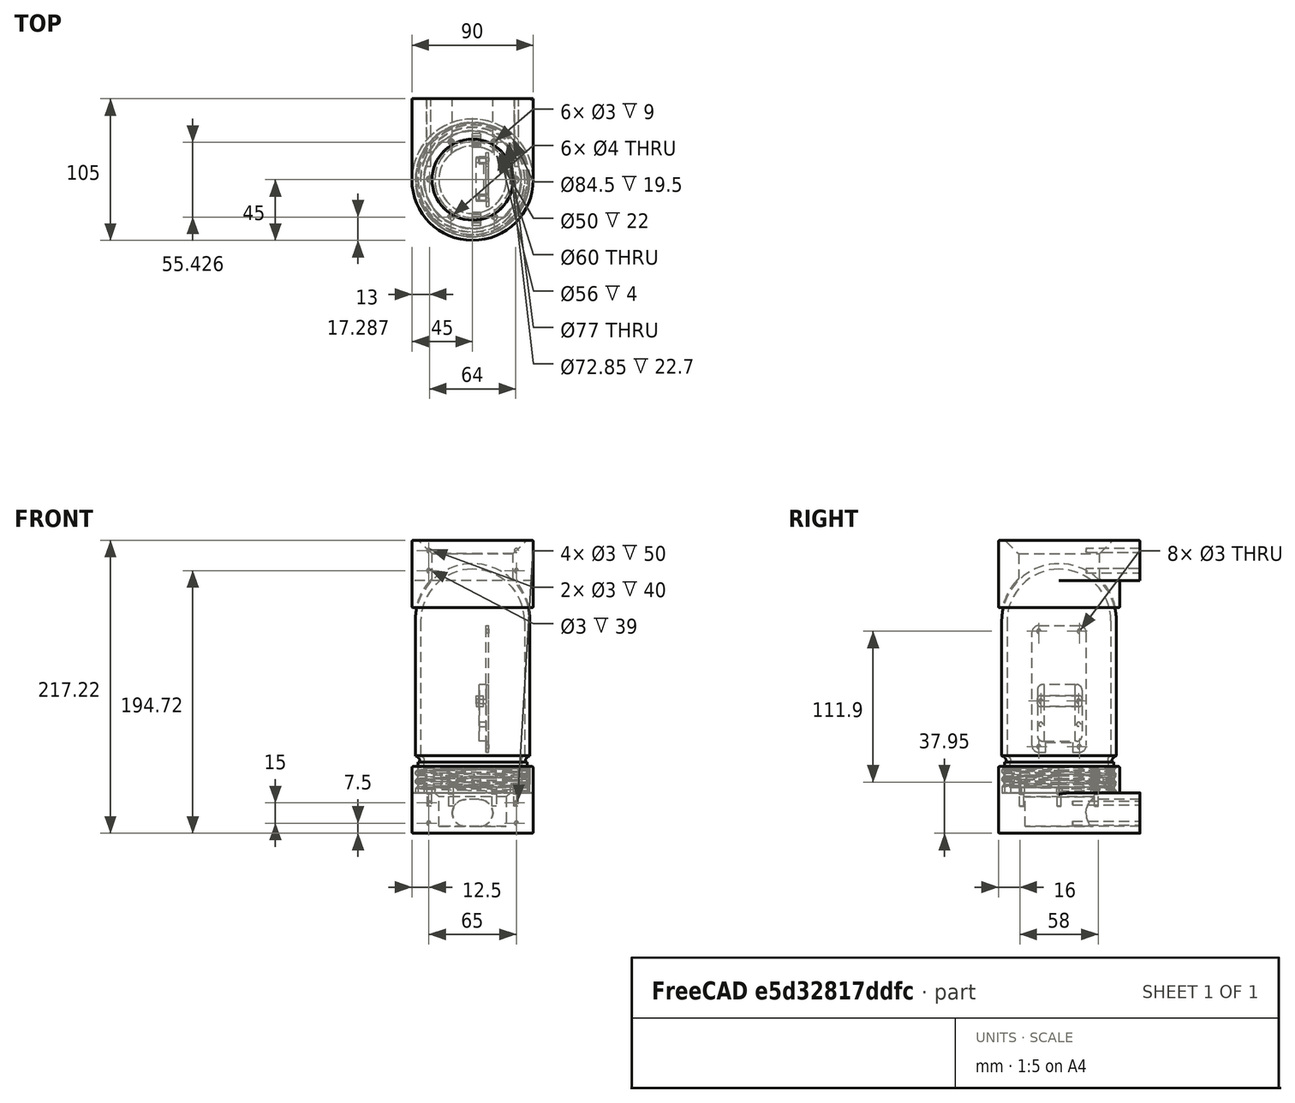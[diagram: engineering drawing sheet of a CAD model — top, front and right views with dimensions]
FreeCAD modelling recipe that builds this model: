
FCSTD DOCUMENT  (FreeCAD 0.19R)
Label: CrocSaintGerard_V5
License: All rights reserved
LicenseURL: http://en.wikipedia.org/wiki/All_rights_reserved
objects: Sketcher::SketchObject×36, PartDesign::Fillet×19, PartDesign::Pocket×18, PartDesign::Pad×14, PartDesign::Body×12, PartDesign::Chamfer×5, Mesh::Feature×4, PartDesign::Revolution×2, Part::Helix×1, PartDesign::ShapeBinder×1, PartDesign::AdditivePipe×1, PartDesign::LinearPattern×1, PartDesign::Groove×1, App::VRMLObject×1, App::MeasureDistance×1
note: 171 computed .brp shape members not serialized (recipe doc carries the construction recipe); baked Part::Feature solids carry a one-line shape summary decoded from their .brp

FEATURE [Part::Helix] Helix
  Angle = 0
  AttacherType = Attacher::AttachEngine3D
  Height = 6.22
  LocalCoord = 0
  Pitch = 6.23
  Radius = 40.5
  Style = 1
FEATURE [Sketcher::SketchObject] Sketch001  label="sketch_cylindre_base"
  FullyConstrained = true
  MapMode = 5
  Support = -> [XY_Plane]
  sketch-geometry (2):
    g0: Circle CenterX=0 CenterY=0 CenterZ=0 NormalX=0 NormalY=0 NormalZ=1 AngleXU=0 Radius=42.25
    g1: Circle CenterX=0 CenterY=0 CenterZ=0 NormalX=0 NormalY=0 NormalZ=1 AngleXU=0 Radius=45
  constraints (4):
    c: Coincident(g0,g-1)
    c: Coincident(g1,g0)
    c: Radius(g0) = 42.25
    c: Radius(g1) = 45
FEATURE [PartDesign::Pad] Pad  label="cylindre_base"
  Direction = (1,1,1)
  Length = 20
  Length2 = 100
  Profile = -> Sketch001
  Type = 0
FEATURE [Sketcher::SketchObject] Sketch002  label="sketch_profil_dent"
  FullyConstrained = true
  MapMode = 5
  Placement = pos=(0,0,0) rot=(1,0,0;1.5708rad)
  Support = -> [XZ_Plane]
  sketch-geometry (7):
    g0: LineSegment StartX=42.25 StartY=4.40427 StartZ=0 EndX=40.9557 EndY=3.11 EndZ=0
    g1: LineSegment StartX=40.9557 StartY=3.11 StartZ=0 EndX=40.9557 EndY=1.29427 EndZ=0
    g2: LineSegment StartX=40.9557 StartY=1.29427 StartZ=0 EndX=42.25 EndY=0 EndZ=0
    g3: LineSegment StartX=42.25 StartY=4.40427 StartZ=0 EndX=42.25 EndY=6.22 EndZ=0
    g4: LineSegment StartX=42.25 StartY=6.22 StartZ=0 EndX=43.25 EndY=6.22 EndZ=0
    g5: LineSegment StartX=43.25 StartY=6.22 StartZ=0 EndX=43.25 EndY=0 EndZ=0
    g6: LineSegment StartX=43.25 StartY=0 StartZ=0 EndX=42.25 EndY=0 EndZ=0
  constraints (21):
    c: Coincident(g0,g1)
    c: Vertical(g1)
    c: Coincident(g1,g2)
    c: DistanceX(g-2,g2) = 42.25
    c: PointOnObject(g2,g-1)
    c: Coincident(g0,g3)
    c: Vertical(g3)
    c: Coincident(g3,g4)
    c: Horizontal(g4)
    c: Coincident(g4,g5)
    c: PointOnObject(g5,g-1)
    c: Vertical(g5)
    c: Coincident(g5,g6)
    c: Coincident(g6,g2)
    c: DistanceX(g4,g4) = 1
    c: Equal(g3,g1)
    c: Equal(g2,g0)
    c: Angle(g2,g-1) = 0.785398
    c: Equal(g1,g3)
    c: DistanceY(g5,g5) = 6.22
    c: DistanceX(g-2,g0) = 42.25
FEATURE [PartDesign::ShapeBinder] ShapeBinder  label="ShapeBinder-helix"
  Support = -> [Helix]
  TraceSupport = false
FEATURE [PartDesign::AdditivePipe] AdditivePipe  label="filet"
  AuxilleryCurvelinear = true
  AuxillerySpineTangent = false
  BaseFeature = -> Pad
  Binormal = (0,0,0)
  Mode = 2
  Profile = -> Sketch002
  Spine = -> ShapeBinder
  SpineTangent = false
  Transformation = 0
  Transition = 0
FEATURE [PartDesign::LinearPattern] LinearPattern  label="ajout_filets"
  BaseFeature = -> AdditivePipe
  Direction = -> Z_Axis
  Length = 12.46
  Occurrences = 3
  Originals = -> [AdditivePipe]
FEATURE [Sketcher::SketchObject] Sketch003  label="sketch_decoupe_filetage"
  FullyConstrained = true
  MapMode = 5
  Placement = pos=(0,0,0) rot=(1,0,0;1.5708rad)
  Support = -> [XZ_Plane]
  sketch-geometry (4):
    g0: LineSegment StartX=-90 StartY=29.5 StartZ=0 EndX=90 EndY=29.5 EndZ=0
    g1: LineSegment StartX=90 StartY=29.5 StartZ=0 EndX=90 EndY=19.5 EndZ=0
    g2: LineSegment StartX=90 StartY=19.5 StartZ=0 EndX=-90 EndY=19.5 EndZ=0
    g3: LineSegment StartX=-90 StartY=19.5 StartZ=0 EndX=-90 EndY=29.5 EndZ=0
  constraints (11):
    c: Coincident(g0,g1)
    c: Coincident(g1,g2)
    c: Coincident(g2,g3)
    c: Coincident(g3,g0)
    c: Horizontal(g2)
    c: Vertical(g1)
    c: Vertical(g3)
    c: DistanceY(g-1,g1) = 19.5
    c: Symmetric(g0,g0,g-2)
    c: DistanceY(g1,g1) = 10
    c: DistanceX(g0,g0) = 180
FEATURE [PartDesign::Pocket] Pocket  label="decoupe_filetage"
  BaseFeature = -> LinearPattern
  Length = 200
  Length2 = 100
  Midplane = true
  Profile = -> Sketch003
  Type = 0
FEATURE [Sketcher::SketchObject] Sketch008  label="sketch_enceinte_verre"
  FullyConstrained = true
  MapMode = 5
  Support = -> [XY_Plane003]
  sketch-geometry (11):
    g0: ArcOfCircle CenterX=-127.4 CenterY=0 CenterZ=0 NormalX=0 NormalY=0 NormalZ=1 AngleXU=0 Radius=42.5 StartAngle=1.5708 EndAngle=3.14159
    g1: ArcOfCircle CenterX=-127.4 CenterY=0 CenterZ=0 NormalX=0 NormalY=0 NormalZ=1 AngleXU=0 Radius=38.5 StartAngle=1.5708 EndAngle=3.14159
    g2: LineSegment StartX=-127.4 StartY=38.5 StartZ=0 EndX=-27.4 EndY=38.5 EndZ=0
    g3: ArcOfCircle CenterX=-24.2871 CenterY=39.1905 CenterZ=0 NormalX=0 NormalY=0 NormalZ=1 AngleXU=0 Radius=3.18854 StartAngle=3.35987 EndAngle=5.2334
    g4: LineSegment StartX=-22.7 StartY=36.425 StartZ=0 EndX=0 EndY=36.425 EndZ=0
    g5: LineSegment StartX=-127.4 StartY=42.5 StartZ=0 EndX=-27.4 EndY=42.5 EndZ=0
    g6: ArcOfCircle CenterX=-22.7 CenterY=43.802 CenterZ=0 NormalX=0 NormalY=0 NormalZ=1 AngleXU=0 Radius=4.87701 StartAngle=3.41184 EndAngle=4.71239
    g7: LineSegment StartX=-22.7 StartY=38.925 StartZ=0 EndX=-22.7 EndY=40.425 EndZ=0
    g8: LineSegment StartX=-22.7 StartY=40.425 StartZ=0 EndX=0 EndY=40.425 EndZ=0
    g9: LineSegment StartX=0 StartY=40.425 StartZ=0 EndX=0 EndY=36.425 EndZ=0
    g10: LineSegment StartX=-165.9 StartY=4.7e-15 StartZ=0 EndX=-169.9 EndY=5.2e-15 EndZ=0
  constraints (35):
    c: PointOnObject(g0,g-1)
    c: PointOnObject(g0,g-1)
    c: Coincident(g1,g0)
    c: PointOnObject(g1,g-1)
    c: Angle(g1) = 1.5708
    c: Angle(g0) = 1.5708
    c: Tangent(g1,g2) = 1.5708
    c: Coincident(g3,g2)
    c: Coincident(g4,g3)
    c: PointOnObject(g4,g-2)
    c: Horizontal(g4)
    c: Coincident(g5,g0)
    c: Horizontal(g5)
    c: Coincident(g6,g5)
    c: Coincident(g6,g7)
    c: Coincident(g7,g8)
    c: PointOnObject(g8,g-2)
    c: Horizontal(g8)
    c: Coincident(g8,g9)
    c: Coincident(g9,g4)
    c: Coincident(g10,g0)
    c: DistanceX(g10,g10) = 4
    c: Radius(g0) = 42.5
    c: Coincident(g1,g10)
    c: DistanceY(g9,g9) = 4
    c: Perpendicular(g6,g7)
    c: Vertical(g7)
    c: DistanceY(g-1,g4) = 36.425
    c: Equal(g4,g8)
    c: DistanceX(g8,g8) = 22.7
    c: DistanceX(g-2,g5) = -27.4
    c: Equal(g2,g5)
    c: PointOnObject(g3,g6)
    c: DistanceY(g7,g7) = 1.5
    c: DistanceX(g5,g5) = 100
FEATURE [PartDesign::Revolution] Revolution  label="revolution_enceinte_verre"
  AllowMultiFace = false
  Angle = 360
  Axis = (1,0,0)
  Base = (0,0,0)
  Profile = -> Sketch008
  ReferenceAxis = -> Sketch008 [H_Axis]
FEATURE [PartDesign::Body] Body003  label="enceinte_verre"
  Group = -> [Sketch008,Revolution]
  Origin = -> Origin003
  Placement = pos=(-3.8e-15,0,-1.78e-14) rot=(0,1,0;1.5708rad)
  Tip = -> Revolution
FEATURE [Sketcher::SketchObject] Sketch  label="sketch_base"
  ExternalGeometry = -> [Pocket]
  FullyConstrained = true
  MapMode = 5
  Placement = pos=(0,0,0) rot=(1,0,0;3.14159rad)
  Support = -> [Pocket]
  sketch-geometry (4):
    g0: ArcOfCircle CenterX=0 CenterY=0 CenterZ=0 NormalX=0 NormalY=0 NormalZ=1 AngleXU=0 Radius=45 StartAngle=0 EndAngle=3.14159
    g1: LineSegment StartX=-45 StartY=5.5e-15 StartZ=0 EndX=-45 EndY=-60 EndZ=0
    g2: LineSegment StartX=-45 StartY=-60 StartZ=0 EndX=45 EndY=-60 EndZ=0
    g3: LineSegment StartX=45 StartY=-60 StartZ=0 EndX=45 EndY=0 EndZ=0
  constraints (11):
    c: Coincident(g0,g-1)
    c: PointOnObject(g0,g-1)
    c: PointOnObject(g0,g-1)
    c: Tangent(g0,g1) = -1.5708
    c: Coincident(g1,g2)
    c: Horizontal(g2)
    c: Coincident(g2,g3)
    c: Coincident(g3,g0)
    c: Vertical(g3)
    c: Radius(g0) = 45
    c: DistanceY(g1,g1) = 60
FEATURE [PartDesign::Pad] Pad001  label="base"
  BaseFeature = -> Pocket
  Direction = (1,1,1)
  Length = 30
  Length2 = 100
  Profile = -> Sketch
  Type = 0
FEATURE [Sketcher::SketchObject] Sketch009  label="sketch_passage_fils"
  FullyConstrained = true
  MapMode = 5
  Support = -> [Pad001]
  sketch-geometry (1):
    g0: Circle CenterX=0 CenterY=0 CenterZ=0 NormalX=0 NormalY=0 NormalZ=1 AngleXU=0 Radius=25
  constraints (2):
    c: Coincident(g0,g-1)
    c: Radius(g0) = 25
FEATURE [PartDesign::Pocket] Pocket001  label="passage_fils"
  BaseFeature = -> Pad001
  Length = 25
  Length2 = 100
  Profile = -> Sketch009
  Type = 0
FEATURE [Sketcher::SketchObject] Sketch010  label="sketch_passage_fils_vertical"
  ExternalGeometry = -> [Pocket001]
  FullyConstrained = true
  MapMode = 5
  Placement = pos=(0,60,0) rot=(0,0.707107,0.707107;3.14159rad)
  Support = -> [Pocket001]
  sketch-geometry (4):
    g0: ArcOfCircle CenterX=-5 CenterY=-15 CenterZ=0 NormalX=0 NormalY=0 NormalZ=1 AngleXU=0 Radius=10 StartAngle=1.5708 EndAngle=4.71239
    g1: ArcOfCircle CenterX=5 CenterY=-15 CenterZ=0 NormalX=0 NormalY=0 NormalZ=1 AngleXU=0 Radius=10 StartAngle=4.71239 EndAngle=7.85398
    g2: LineSegment StartX=-5 StartY=-25 StartZ=0 EndX=5 EndY=-25 EndZ=0
    g3: LineSegment StartX=-5 StartY=-5 StartZ=0 EndX=5 EndY=-5 EndZ=0
  constraints (9):
    c: Tangent(g0,g3) = 1.5708
    c: Tangent(g0,g2) = -1.5708
    c: Tangent(g2,g1) = -1.5708
    c: Tangent(g3,g1) = 1.5708
    c: Equal(g0,g1)
    c: Symmetric(g0,g1,g-2)
    c: Distance(g1,g-3) = 5
    c: DistanceY(g-1,g1) = -5
    c: DistanceX(g2,g2) = 10
FEATURE [PartDesign::Pocket] Pocket002  label="passage_fils_vertical"
  BaseFeature = -> Pocket001
  Length = 60
  Length2 = 100
  Profile = -> Sketch010
  Type = 0
FEATURE [Sketcher::SketchObject] Sketch011  label="sketch_vis_fixation"
  ExternalGeometry = -> [Pocket002]
  FullyConstrained = true
  MapMode = 5
  Placement = pos=(0,60,0) rot=(0,0.707107,0.707107;3.14159rad)
  Support = -> [Pocket002]
  sketch-geometry (4):
    g0: Circle CenterX=-32.5 CenterY=-7.5 CenterZ=0 NormalX=0 NormalY=0 NormalZ=1 AngleXU=0 Radius=1.5
    g1: Circle CenterX=32.5 CenterY=-7.5 CenterZ=0 NormalX=0 NormalY=0 NormalZ=1 AngleXU=0 Radius=1.5
    g2: Circle CenterX=-32.5 CenterY=-22.5 CenterZ=0 NormalX=0 NormalY=0 NormalZ=1 AngleXU=0 Radius=1.5
    g3: Circle CenterX=32.5 CenterY=-22.5 CenterZ=0 NormalX=0 NormalY=0 NormalZ=1 AngleXU=0 Radius=1.5
  constraints (10):
    c: Symmetric(g1,g0,g-2)
    c: DistanceY(g-1,g0) = -7.5
    c: Distance(g0,g1) = 65
    c: Radius(g0) = 1.5
    c: Equal(g0,g1)
    c: Symmetric(g3,g2,g-2)
    c: Radius(g2) = 1.5
    c: Equal(g2,g3)
    c: Distance(g3,g2) = 65
    c: Distance(g3,g-3) = 7.5
FEATURE [PartDesign::Pocket] Pocket003  label="vis_fixation"
  BaseFeature = -> Pocket002
  Length = 50
  Length2 = 100
  Profile = -> Sketch011
  Type = 0
FEATURE [PartDesign::Chamfer] Chamfer
  Angle = 45
  Base = -> Pocket003 [Edge95]
  BaseFeature = -> Pocket003
  ChamferType = 0
  FlipDirection = false
  Size = 3
  Size2 = 1
  SupportTransform = false
FEATURE [Sketcher::SketchObject] Sketch012  label="sketch_vis_montage_interieur"
  FullyConstrained = true
  MapMode = 5
  Support = -> [Chamfer]
  sketch-geometry (13):
    g0: LineSegment StartX=-16 StartY=27.7128 StartZ=0 EndX=-32 EndY=-3.3857e-12 EndZ=0
    g1: LineSegment StartX=-32 StartY=-3.3857e-12 StartZ=0 EndX=-16 EndY=-27.7128 EndZ=0
    g2: LineSegment StartX=-16 StartY=-27.7128 StartZ=0 EndX=16 EndY=-27.7128 EndZ=0
    g3: LineSegment StartX=16 StartY=-27.7128 StartZ=0 EndX=32 EndY=9.738e-12 EndZ=0
    g4: LineSegment StartX=32 StartY=9.738e-12 StartZ=0 EndX=16 EndY=27.7128 EndZ=0
    g5: LineSegment StartX=16 StartY=27.7128 StartZ=0 EndX=-16 EndY=27.7128 EndZ=0
    g6: Circle CenterX=0 CenterY=0 CenterZ=0 NormalX=0 NormalY=0 NormalZ=1 AngleXU=0 Radius=32
    g7: Circle CenterX=-16 CenterY=27.7128 CenterZ=0 NormalX=0 NormalY=0 NormalZ=1 AngleXU=0 Radius=1.5
    g8: Circle CenterX=16 CenterY=27.7128 CenterZ=0 NormalX=0 NormalY=0 NormalZ=1 AngleXU=0 Radius=1.5
    g9: Circle CenterX=-32 CenterY=-3.3857e-12 CenterZ=0 NormalX=0 NormalY=0 NormalZ=1 AngleXU=0 Radius=1.5
    g10: Circle CenterX=32 CenterY=9.738e-12 CenterZ=0 NormalX=0 NormalY=0 NormalZ=1 AngleXU=0 Radius=1.5
    g11: Circle CenterX=16 CenterY=-27.7128 CenterZ=0 NormalX=0 NormalY=0 NormalZ=1 AngleXU=0 Radius=1.5
    g12: Circle CenterX=-16 CenterY=-27.7128 CenterZ=0 NormalX=0 NormalY=0 NormalZ=1 AngleXU=0 Radius=1.5
  constraints (28):
    c: Coincident(g0,g1)
    c: Coincident(g1,g2)
    c: Coincident(g2,g3)
    c: Coincident(g3,g4)
    c: Coincident(g4,g5)
    c: Coincident(g5,g0)
    c: Equal(g0, g1-g5) x5
    c: PointOnObject(g0,g6)
    c: PointOnObject(g1,g6)
    c: PointOnObject(g2,g6)
    c: PointOnObject(g3,g6)
    c: PointOnObject(g4,g6)
    c: PointOnObject(g5,g6)
    c: Coincident(g6,g-1)
    c: Horizontal(g5)
    c: Radius(g6) = 32
    c: Coincident(g7,g0)
    c: Coincident(g8,g4)
    c: Coincident(g9,g0)
    c: Coincident(g10,g3)
    c: Coincident(g11,g2)
    c: Coincident(g12,g1)
    c: Radius(g11) = 1.5
    c: Equal(g11,g12)
    c: Equal(g11,g9)
    c: Equal(g11,g7)
    c: Equal(g11,g8)
    c: Equal(g11,g10)
FEATURE [PartDesign::Pocket] Pocket004  label="vis_montage_interieur"
  BaseFeature = -> Chamfer
  Length = 10
  Length2 = 100
  Profile = -> Sketch012
  Type = 0
FEATURE [PartDesign::Chamfer] Chamfer001
  Angle = 45
  Base = -> Pocket004 [Edge3,Edge2,Edge4,Edge6,Edge8,Edge7]
  BaseFeature = -> Pocket004
  ChamferType = 0
  FlipDirection = false
  Size = 1
  Size2 = 1
  SupportTransform = false
FEATURE [Mesh::Feature] Mesh  label="fixation_enceinte_verre (Meshed)"
FEATURE [Sketcher::SketchObject] Sketch013
  FullyConstrained = true
  MapMode = 5
  Placement = pos=(0,0,0) rot=(0.57735,0.57735,0.57735;2.0944rad)
  Support = -> [YZ_Plane004]
  sketch-geometry (4):
    g0: ArcOfCircle CenterX=0 CenterY=128 CenterZ=0 NormalX=0 NormalY=0 NormalZ=1 AngleXU=0 Radius=43 StartAngle=2.39448 EndAngle=2.92551
    g1: LineSegment StartX=-42 StartY=137.22 StartZ=0 EndX=-45 EndY=137.22 EndZ=0
    g2: LineSegment StartX=-45 StartY=137.22 StartZ=0 EndX=-45 EndY=157.22 EndZ=0
    g3: LineSegment StartX=-45 StartY=157.22 StartZ=0 EndX=-31.5471 EndY=157.22 EndZ=0
  constraints (13):
    c: PointOnObject(g0,g-2)
    c: Coincident(g0,g1)
    c: Coincident(g1,g2)
    c: Vertical(g2)
    c: Coincident(g2,g3)
    c: Coincident(g3,g0)
    c: Horizontal(g3)
    c: Horizontal(g1)
    c: Radius(g0) = 43
    c: DistanceY(g2,g2) = 20
    c: DistanceX(g-2,g1) = -45
    c: DistanceY(g-1,g0) = 128
    c: DistanceX(g1,g1) = 3
FEATURE [PartDesign::Revolution] Revolution001
  Angle = 360
  Axis = (-2e-16,3e-16,1)
  Base = (0,0,0)
  Placement = pos=(0,0,0) rot=(0.57735,0.57735,0.57735;2.0944rad)
  Profile = -> Sketch013
  ReferenceAxis = -> Sketch013 [V_Axis]
FEATURE [Sketcher::SketchObject] Sketch014
  ExternalGeometry = -> [Revolution001]
  FullyConstrained = true
  MapMode = 5
  Placement = pos=(-6.92e-14,4.4e-14,157.22) rot=(0,0,-1;1.5708rad)
  Support = -> [Revolution001]
  sketch-geometry (4):
    g0: ArcOfCircle CenterX=0 CenterY=0 CenterZ=0 NormalX=0 NormalY=0 NormalZ=1 AngleXU=0 Radius=45 StartAngle=4.71239 EndAngle=7.85398
    g1: LineSegment StartX=1.38e-14 StartY=45 StartZ=0 EndX=-60 EndY=45 EndZ=0
    g2: LineSegment StartX=-60 StartY=45 StartZ=0 EndX=-60 EndY=-45 EndZ=0
    g3: LineSegment StartX=-60 StartY=-45 StartZ=0 EndX=-7.1e-15 EndY=-45 EndZ=0
  constraints (10):
    c: Coincident(g0,g-1)
    c: PointOnObject(g0,g-3)
    c: PointOnObject(g0,g-2)
    c: PointOnObject(g0,g-2)
    c: Tangent(g0,g1) = -1.5708
    c: Coincident(g1,g2)
    c: Coincident(g2,g3)
    c: Coincident(g3,g0)
    c: Symmetric(g2,g1,g-1)
    c: DistanceX(g-2,g1) = -60
FEATURE [PartDesign::Pad] Pad002
  BaseFeature = -> Revolution001
  Direction = (1,1,1)
  Length = 30
  Length2 = 100
  Placement = pos=(0,0,0) rot=(0.57735,0.57735,0.57735;2.0944rad)
  Profile = -> Sketch014
  Type = 0
FEATURE [Sketcher::SketchObject] Sketch015
  ExternalGeometry = -> [Pad002]
  FullyConstrained = true
  MapMode = 5
  Placement = pos=(0,0,0) rot=(0.57735,0.57735,0.57735;2.0944rad)
  Support = -> [YZ_Plane004]
  sketch-geometry (3):
    g0: ArcOfCircle CenterX=2.84e-14 CenterY=128 CenterZ=0 NormalX=0 NormalY=0 NormalZ=1 AngleXU=0 Radius=43 StartAngle=1.5708 EndAngle=2.39448
    g1: LineSegment StartX=-31.5471 StartY=157.22 StartZ=0 EndX=3.6e-15 EndY=157.22 EndZ=0
    g2: LineSegment StartX=3.6e-15 StartY=157.22 StartZ=0 EndX=3.6e-15 EndY=171 EndZ=0
  constraints (8):
    c: Coincident(g0,g-3)
    c: Coincident(g0,g-3)
    c: PointOnObject(g0,g-2)
    c: Coincident(g0,g1)
    c: Coincident(g1,g2)
    c: Coincident(g2,g0)
    c: Vertical(g2)
    c: Horizontal(g1)
FEATURE [PartDesign::Groove] Groove
  Angle = 360
  Axis = (-2e-16,3e-16,1)
  Base = (0,0,0)
  BaseFeature = -> Pad002
  Placement = pos=(0,0,0) rot=(0.57735,0.57735,0.57735;2.0944rad)
  Profile = -> Sketch015
  ReferenceAxis = -> Sketch015 [V_Axis]
  Reversed = true
FEATURE [PartDesign::Fillet] Fillet
  Base = -> Chamfer001 [Edge116,Edge168,Edge182,Edge171,Edge181,Edge166]
  BaseFeature = -> Chamfer001
  Radius = 1
  SupportTransform = false
FEATURE [PartDesign::Body] Body  label="fixation_enceinte_verre"
  Group = -> [Sketch001,Pad,Sketch002,ShapeBinder,AdditivePipe,LinearPattern,Sketch003,Pocket,Sketch,Pad001,Sketch009,Pocket001,Sketch010,Pocket002,Sketch011,Pocket003,Chamfer,Sketch012,Pocket004,Chamfer001,Fillet]
  Origin = -> Origin
  Tip = -> Fillet
FEATURE [Sketcher::SketchObject] Sketch019
  FullyConstrained = true
  MapMode = 5
  Support = -> [XY_Plane005]
  sketch-geometry (15):
    g0: Circle CenterX=0 CenterY=0 CenterZ=0 NormalX=0 NormalY=0 NormalZ=1 AngleXU=0 Radius=28
    g1: Circle CenterX=0 CenterY=0 CenterZ=0 NormalX=0 NormalY=0 NormalZ=1 AngleXU=0 Radius=36
    g2: LineSegment StartX=-32 StartY=0 StartZ=0 EndX=-16 EndY=-27.7128 EndZ=0
    g3: LineSegment StartX=-16 StartY=-27.7128 StartZ=0 EndX=16 EndY=-27.7128 EndZ=0
    g4: LineSegment StartX=16 StartY=-27.7128 StartZ=0 EndX=32 EndY=-3.2792e-12 EndZ=0
    g5: LineSegment StartX=32 StartY=-3.2792e-12 StartZ=0 EndX=16 EndY=27.7128 EndZ=0
    g6: LineSegment StartX=16 StartY=27.7128 StartZ=0 EndX=-16 EndY=27.7128 EndZ=0
    g7: LineSegment StartX=-16 StartY=27.7128 StartZ=0 EndX=-32 EndY=0 EndZ=0
    g8: Circle CenterX=0 CenterY=0 CenterZ=0 NormalX=0 NormalY=0 NormalZ=1 AngleXU=0 Radius=32
    g9: Circle CenterX=-16 CenterY=27.7128 CenterZ=0 NormalX=0 NormalY=0 NormalZ=1 AngleXU=0 Radius=2
    g10: Circle CenterX=16 CenterY=27.7128 CenterZ=0 NormalX=0 NormalY=0 NormalZ=1 AngleXU=0 Radius=2
    g11: Circle CenterX=32 CenterY=-3.2792e-12 CenterZ=0 NormalX=0 NormalY=0 NormalZ=1 AngleXU=0 Radius=2
    g12: Circle CenterX=16 CenterY=-27.7128 CenterZ=0 NormalX=0 NormalY=0 NormalZ=1 AngleXU=0 Radius=2
    g13: Circle CenterX=-16 CenterY=-27.7128 CenterZ=0 NormalX=0 NormalY=0 NormalZ=1 AngleXU=0 Radius=2
    g14: Circle CenterX=-32 CenterY=0 CenterZ=0 NormalX=0 NormalY=0 NormalZ=1 AngleXU=0 Radius=2
  constraints (28):
    c: Radius(g0) = 28
    c: Radius(g1) = 36
    c: Coincident(g0,g1)
    c: Coincident(g0,g-1)
    c: Coincident(g2,g3)
    c: Coincident(g3,g4)
    c: Coincident(g4,g5)
    c: Coincident(g5,g6)
    c: Coincident(g6,g7)
    c: Coincident(g7,g2)
    c: Equal(g2, g3-g7) x5
    c: PointOnObject(g2,g8)
    c: PointOnObject(g3,g8)
    c: PointOnObject(g4,g8)
    c: PointOnObject(g5,g8)
    c: PointOnObject(g6,g8)
    c: PointOnObject(g7,g8)
    c: Coincident(g8,g0)
    c: PointOnObject(g7,g-1)
    c: Radius(g8) = 32
    c: Coincident(g9,g6)
    c: Coincident(g10,g5)
    c: Coincident(g11,g4)
    c: Coincident(g12,g3)
    c: Coincident(g13,g2)
    c: Coincident(g14,g2)
    c: Radius(g9) = 2
    c: Equal(g9, g10-g14) x5
FEATURE [PartDesign::Pad] Pad003
  Direction = (1,1,1)
  Length = 4
  Length2 = 100
  Profile = -> Sketch019
  Type = 0
FEATURE [Sketcher::SketchObject] Sketch021
  FullyConstrained = true
  MapMode = 5
  Placement = pos=(-1.179e-13,8.24e-14,187.22) rot=(0,0,-1;1.5708rad)
  Support = -> [Pad002]
  sketch-geometry (1):
    g0: Circle CenterX=0 CenterY=0 CenterZ=0 NormalX=0 NormalY=0 NormalZ=1 AngleXU=0 Radius=30
  constraints (2):
    c: Coincident(g0,g-1)
    c: Radius(g0) = 30
FEATURE [PartDesign::Pocket] Pocket009
  BaseFeature = -> Groove
  Length = 46
  Length2 = 100
  Placement = pos=(0,0,0) rot=(0.57735,0.57735,0.57735;2.0944rad)
  Profile = -> Sketch021
  Type = 0
FEATURE [Sketcher::SketchObject] Sketch022
  FullyConstrained = false
  MapMode = 5
  Placement = pos=(2.7e-14,60,-7e-14) rot=(0.57735,0.57735,0.57735;4.18879rad)
  sketch-geometry (4):
    g0: Circle CenterX=164.72 CenterY=32.5 CenterZ=0 NormalX=0 NormalY=0 NormalZ=1 AngleXU=0 Radius=1.5
    g1: Circle CenterX=179.72 CenterY=32.5 CenterZ=0 NormalX=0 NormalY=0 NormalZ=1 AngleXU=0 Radius=1.5
    g2: Circle CenterX=164.72 CenterY=-32.5 CenterZ=0 NormalX=0 NormalY=0 NormalZ=1 AngleXU=0 Radius=1.5
    g3: Circle CenterX=179.72 CenterY=-32.5 CenterZ=0 NormalX=0 NormalY=0 NormalZ=1 AngleXU=0 Radius=1.5
  constraints (8):
    c: Symmetric(g3,g1,g-1)
    c: Symmetric(g0,g2,g-1)
    c: Distance(g0,g2) = 65
    c: Distance(g3,g1) = 65
    c: Radius(g0) = 1.5
    c: Equal(g0,g1)
    c: Equal(g0,g2)
    c: Equal(g0,g3)
FEATURE [PartDesign::Pocket] Pocket010
  BaseFeature = -> Pocket009
  Length = 40
  Length2 = 100
  Placement = pos=(0,0,0) rot=(0.57735,0.57735,0.57735;2.0944rad)
  Profile = -> Sketch022
  Type = 0
FEATURE [PartDesign::Fillet] Fillet001
  Base = -> Pocket010 [Edge10,Edge27]
  BaseFeature = -> Pocket010
  Placement = pos=(0,0,0) rot=(0.57735,0.57735,0.57735;2.0944rad)
  Radius = 1
  SupportTransform = false
FEATURE [PartDesign::Fillet] Fillet002
  Base = -> Fillet001 [Edge5,Edge21]
  BaseFeature = -> Fillet001
  Placement = pos=(0,0,0) rot=(0.57735,0.57735,0.57735;2.0944rad)
  Radius = 1
  SupportTransform = false
FEATURE [PartDesign::Chamfer] Chamfer002
  Angle = 45
  Base = -> Fillet002 [Edge19]
  BaseFeature = -> Fillet002
  ChamferType = 0
  FlipDirection = false
  Placement = pos=(0,0,0) rot=(0.57735,0.57735,0.57735;2.0944rad)
  Size = 10
  Size2 = 1
  SupportTransform = false
FEATURE [PartDesign::Fillet] Fillet003
  Base = -> Chamfer002 [Edge2]
  BaseFeature = -> Chamfer002
  Placement = pos=(0,0,0) rot=(0.57735,0.57735,0.57735;2.0944rad)
  Radius = 1
  SupportTransform = false
FEATURE [PartDesign::Fillet] Fillet004
  Base = -> Fillet003 [Edge46,Edge5,Edge34]
  BaseFeature = -> Fillet003
  Placement = pos=(0,0,0) rot=(0.57735,0.57735,0.57735;2.0944rad)
  Radius = 1
  SupportTransform = false
FEATURE [PartDesign::Body] Body004  label="tete"
  Group = -> [Sketch013,Revolution001,Sketch014,Pad002,Sketch015,Groove,Sketch021,Pocket009,Sketch022,Pocket010,Fillet001,Fillet002,Chamfer002,Fillet003,Fillet004]
  Origin = -> Origin004
  Tip = -> Fillet004
FEATURE [Mesh::Feature] Mesh001  label="tete (Meshed)"
FEATURE [Sketcher::SketchObject] Sketch005
  FullyConstrained = false
  MapMode = 5
  Placement = pos=(0,0,0) rot=(0.57735,0.57735,0.57735;2.0944rad)
  Support = -> [YZ_Plane002]
  sketch-geometry (8):
    g0: LineSegment StartX=-17 StartY=-5 StartZ=0 EndX=-11.875 EndY=-5 EndZ=0
    g1: LineSegment StartX=-11.875 StartY=-5 StartZ=0 EndX=-11.875 EndY=-1.6 EndZ=0
    g2: LineSegment StartX=-11.875 StartY=-1.6 StartZ=0 EndX=10.875 EndY=-1.6 EndZ=0
    g3: LineSegment StartX=10.875 StartY=-1.6 StartZ=0 EndX=10.875 EndY=-5 EndZ=0
    g4: LineSegment StartX=10.875 StartY=-5 StartZ=0 EndX=16 EndY=-5 EndZ=0
    g5: LineSegment StartX=16 StartY=-5 StartZ=0 EndX=16 EndY=-7 EndZ=0
    g6: LineSegment StartX=16 StartY=-7 StartZ=0 EndX=-17 EndY=-7 EndZ=0
    g7: LineSegment StartX=-17 StartY=-7 StartZ=0 EndX=-17 EndY=-5 EndZ=0
  constraints (24):
    c: Horizontal(g0)
    c: Coincident(g0,g1)
    c: Vertical(g1)
    c: Coincident(g1,g2)
    c: Horizontal(g2)
    c: Coincident(g2,g3)
    c: Vertical(g3)
    c: Coincident(g3,g4)
    c: Horizontal(g4)
    c: Coincident(g4,g5)
    c: Vertical(g5)
    c: Coincident(g5,g6)
    c: Horizontal(g6)
    c: Coincident(g6,g7)
    c: Coincident(g7,g0)
    c: Vertical(g7)
    c: DistanceY(g7,g7) = 2
    c: DistanceY(g1,g1) = 3.4
    c: DistanceX(g2,g2) = 22.75
    c: DistanceX(g0,g0) = 5.125
    c: Equal(g0,g4)
    c: Equal(g5,g7)
    c: DistanceY(g-1,g0) = -5
    c: DistanceX(g-2,g6) = -17
FEATURE [PartDesign::Pad] Pad010
  AllowMultiFace = false
  Direction = (1,1,1)
  Length = 8
  Length2 = 100
  Placement = pos=(0,0,0) rot=(0.57735,0.57735,0.57735;2.0944rad)
  Profile = -> Sketch005
  Type = 0
FEATURE [Sketcher::SketchObject] Sketch006
  ExternalGeometry = -> [Pad010]
  FullyConstrained = true
  MapMode = 5
  Placement = pos=(2e-15,-3.1e-15,-7) rot=(0.707107,0.707107,0;3.14159rad)
  Support = -> [Pad010]
  sketch-geometry (2):
    g0: Circle CenterX=-14.5 CenterY=4 CenterZ=0 NormalX=0 NormalY=0 NormalZ=1 AngleXU=0 Radius=1.5
    g1: Circle CenterX=13.5 CenterY=4 CenterZ=0 NormalX=0 NormalY=0 NormalZ=1 AngleXU=0 Radius=1.5
  constraints (6):
    c: Radius(g1) = 1.5
    c: Equal(g1,g0)
    c: DistanceY(g-1,g1) = 4
    c: DistanceY(g-1,g0) = 4
    c: Distance(g0,g-3) = 2.5
    c: Distance(g1,g-4) = 2.5
FEATURE [PartDesign::Pocket] Pocket013
  AllowMultiFace = false
  BaseFeature = -> Pad010
  Length = 5
  Length2 = 100
  Placement = pos=(0,0,0) rot=(0.57735,0.57735,0.57735;2.0944rad)
  Profile = -> Sketch006
  Type = 0
FEATURE [PartDesign::Fillet] Fillet007
  Base = -> Pocket013 [Edge8,Edge7,Edge19,Edge13]
  BaseFeature = -> Pocket013
  Placement = pos=(0,0,0) rot=(0.57735,0.57735,0.57735;2.0944rad)
  Radius = 2
  SupportTransform = false
FEATURE [PartDesign::Body] Body002  label="Attache"
  Group = -> [Sketch005,Pad010,Sketch006,Pocket013,Fillet007]
  Origin = -> Origin002
  Placement = pos=(9.75,-3e-15,64) rot=(0.707107,0,0.707107;3.14159rad)
  Tip = -> Fillet007
FEATURE [App::VRMLObject] CroqueLivreSaintGerard2021_V1
  Placement = pos=(-16,93.8,-73.5) rot=(0,1,0;-1.5708rad)
  Resources = CroqueLivreSaintGerard2021_V1/CP_Radial_D12.5mm_P5.00mm.wrl | CroqueLivreSaintGerard2021_V1/ | CroqueLivreSaintGerard2021_V1/ | CroqueLivreSaintGerard2021_V1/ | CroqueLivreSaintGerard2021_V1/ | CroqueLivreSaintGerard2021_V1/ | CroqueLivreSaintGerard2021_V1/ | CroqueLivreSaintGerard2021_V1/ | CroqueLivreSaintGerard2021_V1/ | CroqueLivreSaintGerard2021_V1/ | CroqueLivreSaintGerard2021_V1/ | CroqueLivreSaintGerard2021_V1/
FEATURE [Sketcher::SketchObject] Sketch025
  FullyConstrained = true
  MapMode = 5
  Support = -> [XY_Plane006]
  sketch-geometry (17):
    g0: LineSegment StartX=-47 StartY=20 StartZ=0 EndX=47 EndY=20 EndZ=0
    g1: LineSegment StartX=47 StartY=20 StartZ=0 EndX=47 EndY=-20 EndZ=0
    g2: LineSegment StartX=47 StartY=-20 StartZ=0 EndX=-47 EndY=-20 EndZ=0
    g3: LineSegment StartX=-39.75 StartY=18.75 StartZ=0 EndX=39.75 EndY=18.75 EndZ=0
    g4: LineSegment StartX=39.75 StartY=18.75 StartZ=0 EndX=39.75 EndY=-18.75 EndZ=0
    g5: LineSegment StartX=39.75 StartY=-18.75 StartZ=0 EndX=-39.75 EndY=-18.75 EndZ=0
    g6: LineSegment StartX=-39.75 StartY=-18.75 StartZ=0 EndX=-39.75 EndY=18.75 EndZ=0
    g7: Circle CenterX=-42.85 CenterY=15 CenterZ=0 NormalX=0 NormalY=0 NormalZ=1 AngleXU=0 Radius=1.5
    g8: Circle CenterX=-42.85 CenterY=-15 CenterZ=0 NormalX=0 NormalY=0 NormalZ=1 AngleXU=0 Radius=1.5
    g9: Circle CenterX=42.85 CenterY=-15 CenterZ=0 NormalX=0 NormalY=0 NormalZ=1 AngleXU=0 Radius=1.5
    g10: Circle CenterX=42.85 CenterY=15 CenterZ=0 NormalX=0 NormalY=0 NormalZ=1 AngleXU=0 Radius=1.5
    g11: Circle CenterX=-42.85 CenterY=15 CenterZ=0 NormalX=0 NormalY=0 NormalZ=1 AngleXU=0 Radius=3
    g12: LineSegment StartX=-47 StartY=20 StartZ=0 EndX=-47 EndY=10 EndZ=0
    g13: LineSegment StartX=-47 StartY=10 StartZ=0 EndX=-39.75 EndY=10 EndZ=0
    g14: LineSegment StartX=-39.75 StartY=10 StartZ=0 EndX=-39.75 EndY=-10 EndZ=0
    g15: LineSegment StartX=-39.75 StartY=-10 StartZ=0 EndX=-47 EndY=-10 EndZ=0
    g16: LineSegment StartX=-47 StartY=-10 StartZ=0 EndX=-47 EndY=-20 EndZ=0
  constraints (44):
    c: Coincident(g0,g1)
    c: Coincident(g1,g2)
    c: Horizontal(g0)
    c: Horizontal(g2)
    c: Vertical(g1)
    c: Symmetric(g0,g1,g-1)
    c: DistanceY(g1,g1) = 40
    c: DistanceX(g0,g0) = 94
    c: Coincident(g3,g4)
    c: Coincident(g4,g5)
    c: Coincident(g5,g6)
    c: Coincident(g6,g3)
    c: Horizontal(g3)
    c: Horizontal(g5)
    c: Vertical(g4)
    c: Vertical(g6)
    c: Symmetric(g3,g4,g-1)
    c: DistanceY(g6,g6) = 37.5
    c: DistanceX(g3,g3) = 79.5
    c: Radius(g10) = 1.5
    c: Equal(g10,g9)
    c: Equal(g10,g8)
    c: Equal(g10,g7)
    c: Symmetric(g7,g8,g-1)
    c: Symmetric(g10,g9,g-1)
    c: Symmetric(g10,g7,g-2)
    c: Coincident(g11,g7)
    c: Radius(g11) = 3
    c: Coincident(g0,g12)
    c: Vertical(g12)
    c: Coincident(g12,g13)
    c: Horizontal(g13)
    c: Coincident(g13,g14)
    c: Vertical(g14)
    c: Coincident(g14,g15)
    c: Horizontal(g15)
    c: Coincident(g15,g16)
    c: Coincident(g16,g2)
    c: Vertical(g16)
    c: Symmetric(g15,g12,g-1)
    c: PointOnObject(g13,g6)
    c: DistanceY(g14,g14) = 20
    c: DistanceY(g-1,g7) = 15
    c: DistanceX(g-2,g7) = -42.85
FEATURE [PartDesign::Pad] Pad011
  AllowMultiFace = false
  Direction = (1,1,1)
  Length = 2
  Length2 = 100
  Profile = -> Sketch025
  Type = 0
FEATURE [PartDesign::Fillet] Fillet006
  Base = -> Pad011 [Edge8,Edge5,Edge11,Edge1]
  BaseFeature = -> Pad011
  Radius = 5
  SupportTransform = false
FEATURE [Sketcher::SketchObject] Sketch024
  ExternalGeometry = -> [Fillet006]
  FullyConstrained = true
  MapMode = 5
  Placement = pos=(0,0,0) rot=(1,0,0;3.14159rad)
  Support = -> [Fillet006]
  sketch-geometry (4):
    g0: LineSegment StartX=-38.75 StartY=12 StartZ=0 EndX=3.25 EndY=12 EndZ=0
    g1: LineSegment StartX=3.25 StartY=12 StartZ=0 EndX=3.25 EndY=-11 EndZ=0
    g2: LineSegment StartX=3.25 StartY=-11 StartZ=0 EndX=-38.75 EndY=-11 EndZ=0
    g3: LineSegment StartX=-38.75 StartY=-11 StartZ=0 EndX=-38.75 EndY=12 EndZ=0
  constraints (12):
    c: Coincident(g0,g1)
    c: Coincident(g1,g2)
    c: Coincident(g2,g3)
    c: Coincident(g3,g0)
    c: Horizontal(g0)
    c: Horizontal(g2)
    c: Vertical(g1)
    c: Vertical(g3)
    c: DistanceY(g1,g1) = 23
    c: DistanceX(g0,g0) = 42
    c: DistanceY(g-1,g0) = 12
    c: Distance(g0,g-3) = 1
FEATURE [PartDesign::Pocket] Pocket012
  AllowMultiFace = false
  BaseFeature = -> Fillet006
  Length = 1.5
  Length2 = 100
  Profile = -> Sketch024
  Type = 0
FEATURE [Sketcher::SketchObject] Sketch026
  FullyConstrained = true
  MapMode = 5
  Support = -> [XY_Plane001]
  sketch-geometry (16):
    g0: LineSegment StartX=-47 StartY=20 StartZ=0 EndX=47 EndY=20 EndZ=0
    g1: LineSegment StartX=47 StartY=20 StartZ=0 EndX=47 EndY=-20 EndZ=0
    g2: LineSegment StartX=47 StartY=-20 StartZ=0 EndX=-47 EndY=-20 EndZ=0
    g3: LineSegment StartX=-47 StartY=-20 StartZ=0 EndX=-47 EndY=20 EndZ=0
    g4: Circle CenterX=-42.85 CenterY=15 CenterZ=0 NormalX=0 NormalY=0 NormalZ=1 AngleXU=0 Radius=1.5
    g5: Circle CenterX=-42.85 CenterY=-15 CenterZ=0 NormalX=0 NormalY=0 NormalZ=1 AngleXU=0 Radius=1.5
    g6: Circle CenterX=42.85 CenterY=15 CenterZ=0 NormalX=0 NormalY=0 NormalZ=1 AngleXU=0 Radius=1.5
    g7: Circle CenterX=42.85 CenterY=-15 CenterZ=0 NormalX=0 NormalY=0 NormalZ=1 AngleXU=0 Radius=1.5
    g8: LineSegment StartX=-32.25 StartY=15.5 StartZ=0 EndX=37.75 EndY=15.5 EndZ=0
    g9: LineSegment StartX=37.75 StartY=15.5 StartZ=0 EndX=37.75 EndY=-15.5 EndZ=0
    g10: LineSegment StartX=37.75 StartY=-15.5 StartZ=0 EndX=-32.25 EndY=-15.5 EndZ=0
    g11: LineSegment StartX=-32.25 StartY=-15.5 StartZ=0 EndX=-32.25 EndY=15.5 EndZ=0
    g12: LineSegment StartX=-39.75 StartY=18.75 StartZ=0 EndX=39.75 EndY=18.75 EndZ=0
    g13: LineSegment StartX=39.75 StartY=18.75 StartZ=0 EndX=39.75 EndY=-18.75 EndZ=0
    g14: LineSegment StartX=39.75 StartY=-18.75 StartZ=0 EndX=-39.75 EndY=-18.75 EndZ=0
    g15: LineSegment StartX=-39.75 StartY=-18.75 StartZ=0 EndX=-39.75 EndY=18.75 EndZ=0
  constraints (42):
    c: Coincident(g0,g1)
    c: Coincident(g1,g2)
    c: Coincident(g2,g3)
    c: Coincident(g3,g0)
    c: Horizontal(g0)
    c: Horizontal(g2)
    c: Vertical(g1)
    c: Vertical(g3)
    c: Symmetric(g1,g0,g-1)
    c: DistanceX(g0,g0) = 94
    c: DistanceY(g3,g3) = 40
    c: Radius(g4) = 1.5
    c: Equal(g4,g6)
    c: Equal(g4,g5)
    c: Equal(g4,g7)
    c: Symmetric(g5,g4,g-1)
    c: Symmetric(g6,g7,g-1)
    c: Symmetric(g4,g6,g-2)
    c: DistanceY(g-1,g4) = 15
    c: DistanceX(g-2,g4) = -42.85
    c: Coincident(g8,g9)
    c: Coincident(g9,g10)
    c: Coincident(g10,g11)
    c: Coincident(g11,g8)
    c: Horizontal(g8)
    c: Horizontal(g10)
    c: Vertical(g11)
    c: DistanceY(g9,g9) = 31
    c: DistanceX(g8,g8) = 70
    c: Symmetric(g8,g9,g-1)
    c: Coincident(g12,g13)
    c: Coincident(g13,g14)
    c: Coincident(g14,g15)
    c: Coincident(g15,g12)
    c: Horizontal(g12)
    c: Horizontal(g14)
    c: Vertical(g13)
    c: Vertical(g15)
    c: DistanceX(g12,g12) = 79.5
    c: Symmetric(g12,g13,g-1)
    c: DistanceY(g15,g15) = 37.5
    c: Distance(g8,g13) = 2
FEATURE [PartDesign::Pad] Pad009
  AllowMultiFace = false
  Direction = (1,1,1)
  Length = 3
  Length2 = 100
  Profile = -> Sketch026
  Type = 0
FEATURE [Sketcher::SketchObject] Sketch023
  FullyConstrained = true
  MapMode = 5
  Placement = pos=(0,0,0) rot=(1,0,0;3.14159rad)
  Support = -> [Pad009]
  sketch-geometry (4):
    g0: LineSegment StartX=-39.75 StartY=18.75 StartZ=0 EndX=39.75 EndY=18.75 EndZ=0
    g1: LineSegment StartX=39.75 StartY=18.75 StartZ=0 EndX=39.75 EndY=-18.75 EndZ=0
    g2: LineSegment StartX=39.75 StartY=-18.75 StartZ=0 EndX=-39.75 EndY=-18.75 EndZ=0
    g3: LineSegment StartX=-39.75 StartY=-18.75 StartZ=0 EndX=-39.75 EndY=18.75 EndZ=0
  constraints (11):
    c: Coincident(g0,g1)
    c: Coincident(g1,g2)
    c: Coincident(g2,g3)
    c: Coincident(g3,g0)
    c: Horizontal(g0)
    c: Horizontal(g2)
    c: Vertical(g1)
    c: Vertical(g3)
    c: DistanceY(g1,g1) = 37.5
    c: DistanceX(g0,g0) = 79.5
    c: Symmetric(g0,g2,g-1)
FEATURE [PartDesign::Pocket] Pocket011
  AllowMultiFace = false
  BaseFeature = -> Pad009
  Length = 1.5
  Length2 = 100
  Profile = -> Sketch023
  Type = 0
FEATURE [PartDesign::Fillet] Fillet005
  Base = -> Pocket011 [Edge5,Edge1,Edge8,Edge2]
  BaseFeature = -> Pocket011
  Radius = 5
  SupportTransform = false
FEATURE [PartDesign::Chamfer] Chamfer003
  Angle = 45
  Base = -> Fillet005 [Edge33,Edge34,Edge35,Edge36]
  BaseFeature = -> Fillet005
  ChamferType = 0
  FlipDirection = false
  Size = 2
  Size2 = 1
  SupportTransform = false
FEATURE [PartDesign::Body] Body001  label="Devant"
  Group = -> [Sketch026,Pad009,Sketch023,Pocket011,Fillet005,Chamfer003]
  Origin = -> Origin001
  Placement = pos=(12,-3.4e-15,77) rot=(-0.707107,0,-0.707107;3.14159rad)
  Tip = -> Chamfer003
FEATURE [Sketcher::SketchObject] Sketch030
  ExternalGeometry = -> [Pocket012]
  FullyConstrained = true
  MapMode = 5
  Placement = pos=(0,0,0) rot=(1,0,0;3.14159rad)
  Support = -> [Pocket012]
  sketch-geometry (12):
    g0: LineSegment StartX=-38.75 StartY=12 StartZ=0 EndX=3.25 EndY=12 EndZ=0
    g1: LineSegment StartX=3.25 StartY=12 StartZ=0 EndX=3.25 EndY=17 EndZ=0
    g2: LineSegment StartX=3.25 StartY=17 StartZ=0 EndX=-38.75 EndY=17 EndZ=0
    g3: LineSegment StartX=-38.75 StartY=17 StartZ=0 EndX=-38.75 EndY=12 EndZ=0
    g4: LineSegment StartX=-38.75 StartY=-11 StartZ=0 EndX=3.25 EndY=-11 EndZ=0
    g5: LineSegment StartX=3.25 StartY=-11 StartZ=0 EndX=3.25 EndY=-16 EndZ=0
    g6: LineSegment StartX=3.25 StartY=-16 StartZ=0 EndX=-38.75 EndY=-16 EndZ=0
    g7: LineSegment StartX=-38.75 StartY=-16 StartZ=0 EndX=-38.75 EndY=-11 EndZ=0
    g8: Circle CenterX=-26.25 CenterY=14.5 CenterZ=0 NormalX=0 NormalY=0 NormalZ=1 AngleXU=0 Radius=1.5
    g9: Circle CenterX=-26.25 CenterY=-13.5 CenterZ=0 NormalX=0 NormalY=0 NormalZ=1 AngleXU=0 Radius=1.5
    g10: Circle CenterX=-9.25 CenterY=14.5 CenterZ=0 NormalX=0 NormalY=0 NormalZ=1 AngleXU=0 Radius=1.5
    g11: Circle CenterX=-9.25 CenterY=-13.5 CenterZ=0 NormalX=0 NormalY=0 NormalZ=1 AngleXU=0 Radius=1.5
  constraints (32):
    c: Coincident(g0,g1)
    c: Coincident(g1,g2)
    c: Coincident(g2,g3)
    c: Coincident(g3,g0)
    c: Horizontal(g2)
    c: Vertical(g1)
    c: Vertical(g3)
    c: Coincident(g0,g-3)
    c: Coincident(g4,g5)
    c: Coincident(g5,g6)
    c: Coincident(g6,g7)
    c: Coincident(g7,g4)
    c: Horizontal(g6)
    c: Vertical(g5)
    c: Vertical(g7)
    c: Coincident(g4,g-4)
    c: Coincident(g4,g-4)
    c: Coincident(g0,g-3)
    c: Equal(g1,g5)
    c: DistanceY(g1,g1) = 5
    c: Radius(g11) = 1.5
    c: Equal(g11,g10)
    c: Equal(g11,g8)
    c: Equal(g11,g9)
    c: Distance(g8,g0) = 2.5
    c: Distance(g10,g0) = 2.5
    c: Distance(g8,g3) = 12.5
    c: Distance(g10,g1) = 12.5
    c: Distance(g9,g4) = 2.5
    c: Distance(g11,g4) = 2.5
    c: Distance(g9,g7) = 12.5
    c: Distance(g11,g5) = 12.5
FEATURE [PartDesign::Pad] Pad008
  BaseFeature = -> Pocket012
  Direction = (1,1,1)
  Length = 5
  Length2 = 100
  Profile = -> Sketch030
  Type = 0
FEATURE [PartDesign::Fillet] Fillet008
  Base = -> Pad008 [Edge55,Edge68,Edge58,Edge66]
  BaseFeature = -> Pad008
  Radius = 4
  SupportTransform = false
FEATURE [PartDesign::Body] Body006  label="Plaque"
  Group = -> [Sketch025,Pad011,Fillet006,Sketch024,Pocket012,Sketch030,Pad008,Fillet008]
  Origin = -> Origin008
  Placement = pos=(10,-3e-15,77) rot=(0.707107,0,0.707107;3.14159rad)
  Tip = -> Fillet008
FEATURE [Sketcher::SketchObject] Sketch034
  FullyConstrained = true
  MapMode = 5
  Placement = pos=(0,0,0) rot=(0.57735,0.57735,0.57735;2.0944rad)
  Support = -> [YZ_Plane009]
  sketch-geometry (24):
    g0: LineSegment StartX=-27.5 StartY=127.5 StartZ=0 EndX=27.5 EndY=127.5 EndZ=0
    g1: LineSegment StartX=-27.5 StartY=127.5 StartZ=0 EndX=-27.5 EndY=119.5 EndZ=0
    g2: LineSegment StartX=-27.5 StartY=119.5 StartZ=0 EndX=-22.5 EndY=119.5 EndZ=0
    g3: LineSegment StartX=-22.5 StartY=119.5 StartZ=0 EndX=-22.5 EndY=34.5 EndZ=0
    g4: LineSegment StartX=22.5 StartY=34.5 StartZ=0 EndX=22.5 EndY=119.5 EndZ=0
    g5: LineSegment StartX=22.5 StartY=119.5 StartZ=0 EndX=27.5 EndY=119.5 EndZ=0
    g6: LineSegment StartX=27.5 StartY=119.5 StartZ=0 EndX=27.5 EndY=127.5 EndZ=0
    g7: Circle CenterX=-23 CenterY=123.5 CenterZ=0 NormalX=0 NormalY=0 NormalZ=1 AngleXU=0 Radius=1.5
    g8: Circle CenterX=-15 CenterY=119.85 CenterZ=0 NormalX=0 NormalY=0 NormalZ=1 AngleXU=0 Radius=1.5
    g9: Circle CenterX=15 CenterY=119.85 CenterZ=0 NormalX=0 NormalY=0 NormalZ=1 AngleXU=0 Radius=1.5
    g10: Circle CenterX=23 CenterY=123.5 CenterZ=0 NormalX=0 NormalY=0 NormalZ=1 AngleXU=0 Radius=1.5
    g11: Circle CenterX=-23 CenterY=30.5 CenterZ=0 NormalX=0 NormalY=0 NormalZ=1 AngleXU=0 Radius=1.5
    g12: Circle CenterX=-15 CenterY=34.15 CenterZ=0 NormalX=0 NormalY=0 NormalZ=1 AngleXU=0 Radius=1.5
    g13: Circle CenterX=15 CenterY=34.15 CenterZ=0 NormalX=0 NormalY=0 NormalZ=1 AngleXU=0 Radius=1.5
    g14: Circle CenterX=23 CenterY=30.5 CenterZ=0 NormalX=0 NormalY=0 NormalZ=1 AngleXU=0 Radius=1.5
    g15: LineSegment StartX=22.5 StartY=34.5 StartZ=0 EndX=27.5 EndY=34.5 EndZ=0
    g16: LineSegment StartX=27.5 StartY=34.5 StartZ=0 EndX=34 EndY=4 EndZ=0
    g17: LineSegment StartX=34 StartY=4 StartZ=0 EndX=25.8203 EndY=4 EndZ=0
    g18: LineSegment StartX=25.8203 StartY=4 StartZ=0 EndX=21.0253 EndY=26.5 EndZ=0
    g19: LineSegment StartX=21.0253 StartY=26.5 StartZ=0 EndX=-21.0253 EndY=26.5 EndZ=0
    g20: LineSegment StartX=-21.0253 StartY=26.5 StartZ=0 EndX=-25.8203 EndY=4 EndZ=0
    g21: LineSegment StartX=-25.8203 StartY=4 StartZ=0 EndX=-34 EndY=4 EndZ=0
    g22: LineSegment StartX=-34 StartY=4 StartZ=0 EndX=-27.5 EndY=34.5 EndZ=0
    g23: LineSegment StartX=-27.5 StartY=34.5 StartZ=0 EndX=-22.5 EndY=34.5 EndZ=0
  constraints (59):
    c: Coincident(g0,g1)
    c: Vertical(g1)
    c: Coincident(g1,g2)
    c: Horizontal(g2)
    c: Coincident(g2,g3)
    c: Vertical(g3)
    c: Vertical(g4)
    c: Coincident(g4,g5)
    c: Horizontal(g5)
    c: Coincident(g5,g6)
    c: Coincident(g6,g0)
    c: Vertical(g6)
    c: Symmetric(g0,g0,g-2)
    c: Radius(g14) = 1.5
    c: Equal(g14,g13)
    c: Equal(g14,g12)
    c: Equal(g14,g11)
    c: Equal(g14, g7-g10) x4
    c: Symmetric(g7,g10,g-2)
    c: Symmetric(g8,g9,g-2)
    c: Symmetric(g12,g13,g-2)
    c: Symmetric(g11,g14,g-2)
    c: Distance(g12,g13) = 30
    c: Distance(g8,g9) = 30
    c: Distance(g8,g0) = 7.65
    c: Distance(g7,g0) = 4
    c: DistanceX(g-2,g7) = -23
    c: DistanceX(g-2,g11) = -23
    c: DistanceY(g6,g6) = 8
    c: DistanceY(g-1,g12) = 34.15
    c: DistanceY(g-1,g11) = 30.5
    c: Symmetric(g2,g4,g-2)
    c: DistanceX(g0,g0) = 55
    c: Coincident(g4,g15)
    c: Horizontal(g15)
    c: Coincident(g15,g16)
    c: Coincident(g16,g17)
    c: Coincident(g17,g18)
    c: Coincident(g18,g19)
    c: Coincident(g19,g20)
    c: Coincident(g20,g21)
    c: Coincident(g21,g22)
    c: Coincident(g22,g23)
    c: Coincident(g23,g3)
    c: Horizontal(g23)
    c: Symmetric(g22,g15,g-2)
    c: Symmetric(g19,g18,g-2)
    c: DistanceX(g2,g2) = 5
    c: Equal(g2,g23)
    c: Distance(g11,g19) = 4
    c: Distance(g3,g19) = 8
    c: DistanceY(g-1,g0) = 127.5
    c: Distance(g19,g22) = 8
    c: Horizontal(g17)
    c: DistanceY(g-1,g16) = 4
    c: Parallel(g18,g16)
    c: DistanceX(g-2,g16) = 34
    c: Symmetric(g21,g16,g-2)
    c: Symmetric(g20,g17,g-2)
FEATURE [PartDesign::Pad] Pad014
  Direction = (1,1,1)
  Length = 4
  Length2 = 100
  Placement = pos=(0,0,0) rot=(0.57735,0.57735,0.57735;2.0944rad)
  Profile = -> Sketch034
  Type = 0
FEATURE [Sketcher::SketchObject] Sketch035
  FullyConstrained = false
  MapMode = 5
  Placement = pos=(-1.39e-14,0,0) rot=(0.57735,0.57735,-0.57735;4.18879rad)
  Support = -> [Pad014]
  sketch-geometry (8):
    g0: LineSegment StartX=17.5 StartY=-37.65 StartZ=0 EndX=17.5 EndY=-114.85 EndZ=0
    g1: LineSegment StartX=17.5 StartY=-114.85 StartZ=0 EndX=-17.5 EndY=-114.85 EndZ=0
    g2: LineSegment StartX=-17.5 StartY=-114.85 StartZ=0 EndX=-17.5 EndY=-37.65 EndZ=0
    g3: LineSegment StartX=-17.5 StartY=-37.65 StartZ=0 EndX=-12 EndY=-37.65 EndZ=0
    g4: LineSegment StartX=-12 StartY=-37.65 StartZ=0 EndX=-12 EndY=-17.65 EndZ=0
    g5: LineSegment StartX=-12 StartY=-17.65 StartZ=0 EndX=12 EndY=-17.65 EndZ=0
    g6: LineSegment StartX=12 StartY=-17.65 StartZ=0 EndX=12 EndY=-37.65 EndZ=0
    g7: LineSegment StartX=12 StartY=-37.65 StartZ=0 EndX=17.5 EndY=-37.65 EndZ=0
  constraints (17):
    c: Coincident(g0,g1)
    c: Coincident(g1,g2)
    c: Vertical(g0)
    c: Symmetric(g0,g1,g-2)
    c: Coincident(g2,g3)
    c: Horizontal(g3)
    c: Coincident(g3,g4)
    c: Vertical(g4)
    c: Coincident(g4,g5)
    c: Horizontal(g5)
    c: Coincident(g5,g6)
    c: Vertical(g6)
    c: Coincident(g6,g7)
    c: Coincident(g7,g0)
    c: Symmetric(g2,g0,g-2)
    c: Symmetric(g6,g3,g-2)
    c: DistanceY(g6,g6) = 20
FEATURE [PartDesign::Pocket] Pocket016
  BaseFeature = -> Pad014
  Length = 13
  Length2 = 100
  Placement = pos=(0,0,0) rot=(0.57735,0.57735,0.57735;2.0944rad)
  Profile = -> Sketch035
  Type = 0
FEATURE [Sketcher::SketchObject] Sketch036
  FullyConstrained = false
  MapMode = 5
  Placement = pos=(-2.77e-14,0,0) rot=(-0.57735,-0.57735,0.57735;2.0944rad)
  Support = -> [Pocket016]
  sketch-geometry (2):
    g0: Circle CenterX=-29 CenterY=-8 CenterZ=0 NormalX=0 NormalY=0 NormalZ=1 AngleXU=0 Radius=1.5
    g1: Circle CenterX=29 CenterY=-8 CenterZ=0 NormalX=0 NormalY=0 NormalZ=1 AngleXU=0 Radius=1.5
  constraints (4):
    c: Radius(g1) = 1.5
    c: Equal(g1,g0)
    c: Symmetric(g1,g0,g-2)
    c: DistanceX(g-2,g1) = 29
FEATURE [PartDesign::Pocket] Pocket017
  BaseFeature = -> Pocket016
  Length = 13
  Length2 = 100
  Placement = pos=(0,0,0) rot=(0.57735,0.57735,0.57735;2.0944rad)
  Profile = -> Sketch036
  Type = 0
FEATURE [PartDesign::Fillet] Fillet012
  Base = -> Pocket017 [Edge84,Edge78,Edge76,Edge73,Edge2,Edge75,Edge92,Edge79]
  BaseFeature = -> Pocket017
  Placement = pos=(0,0,0) rot=(0.57735,0.57735,0.57735;2.0944rad)
  Radius = 3
  SupportTransform = false
FEATURE [PartDesign::Fillet] Fillet013
  Base = -> Fillet012 [Edge115,Edge93]
  BaseFeature = -> Fillet012
  Placement = pos=(0,0,0) rot=(0.57735,0.57735,0.57735;2.0944rad)
  Radius = 3
  SupportTransform = false
FEATURE [PartDesign::Chamfer] Chamfer004
  Angle = 45
  Base = -> Fillet013 [Edge120,Edge132]
  BaseFeature = -> Fillet013
  ChamferType = 0
  FlipDirection = false
  Placement = pos=(0,0,0) rot=(0.57735,0.57735,0.57735;2.0944rad)
  Size = 1.5
  Size2 = 1
  SupportTransform = false
FEATURE [PartDesign::Body] Body009  label="support_plaque_ecran"
  Group = -> [Sketch034,Pad014,Sketch035,Pocket016,Sketch036,Pocket017,Fillet012,Fillet013,Chamfer004]
  Origin = -> Origin010
  Placement = pos=(6,0,0) rot=(0,0,1;0rad)
  Tip = -> Chamfer004
FEATURE [Mesh::Feature] Mesh002  label="support_plaque_ecran (Meshed)"
FEATURE [Sketcher::SketchObject] Sketch037
  ExternalGeometry = -> [Pad003]
  FullyConstrained = true
  MapMode = 5
  Placement = pos=(0,0,4) rot=(0,0,1;0rad)
  Support = -> [Pad003]
  sketch-geometry (8):
    g0: LineSegment StartX=0 StartY=35.4965 StartZ=0 EndX=6 EndY=35.4965 EndZ=0
    g1: LineSegment StartX=6 StartY=35.4965 StartZ=0 EndX=6 EndY=23.4965 EndZ=0
    g2: LineSegment StartX=6 StartY=23.4965 StartZ=0 EndX=0 EndY=23.4965 EndZ=0
    g3: LineSegment StartX=0 StartY=23.4965 StartZ=0 EndX=0 EndY=35.4965 EndZ=0
    g4: LineSegment StartX=0 StartY=-24 StartZ=0 EndX=6 EndY=-24 EndZ=0
    g5: LineSegment StartX=6 StartY=-24 StartZ=0 EndX=6 EndY=-36 EndZ=0
    g6: LineSegment StartX=6 StartY=-36 StartZ=0 EndX=0 EndY=-36 EndZ=0
    g7: LineSegment StartX=0 StartY=-36 StartZ=0 EndX=0 EndY=-24 EndZ=0
  constraints (24):
    c: Coincident(g0,g1)
    c: Coincident(g1,g2)
    c: Coincident(g2,g3)
    c: Coincident(g3,g0)
    c: Horizontal(g0)
    c: Horizontal(g2)
    c: Vertical(g1)
    c: Vertical(g3)
    c: Coincident(g4,g5)
    c: Coincident(g5,g6)
    c: Coincident(g6,g7)
    c: Coincident(g7,g4)
    c: Horizontal(g4)
    c: Horizontal(g6)
    c: Vertical(g5)
    c: Vertical(g7)
    c: PointOnObject(g0,g-2)
    c: DistanceX(g4,g4) = 6
    c: DistanceX(g2,g2) = 6
    c: DistanceY(g3,g3) = 12
    c: DistanceY(g7,g7) = 12
    c: PointOnObject(g0,g-4)
    c: PointOnObject(g4,g-2)
    c: PointOnObject(g6,g-4)
FEATURE [PartDesign::Pad] Pad015
  BaseFeature = -> Pad003
  Direction = (1,1,1)
  Length = 8
  Length2 = 100
  Profile = -> Sketch037
  Type = 0
FEATURE [Sketcher::SketchObject] Sketch038
  FullyConstrained = false
  MapMode = 5
  Placement = pos=(6,0,0) rot=(0.57735,0.57735,0.57735;2.0944rad)
  Support = -> [Pad015]
  sketch-geometry (15):
    g0: LineSegment StartX=35.4965 StartY=4 StartZ=0 EndX=34.0144 EndY=4 EndZ=0
    g1: LineSegment StartX=34.0144 StartY=4 StartZ=0 EndX=32.3432 EndY=12 EndZ=0
    g2: LineSegment StartX=32.3432 StartY=12 StartZ=0 EndX=35.4965 EndY=12 EndZ=0
    g3: LineSegment StartX=35.4965 StartY=12 StartZ=0 EndX=35.4965 EndY=4 EndZ=0
    g4: LineSegment StartX=23.4965 StartY=4 StartZ=0 EndX=25.8363 EndY=4 EndZ=0
    g5: LineSegment StartX=25.8363 StartY=4 StartZ=0 EndX=24.094 EndY=12 EndZ=0
    g6: LineSegment StartX=24.094 StartY=12 StartZ=0 EndX=23.4965 EndY=12 EndZ=0
    g7: LineSegment StartX=23.4965 StartY=12 StartZ=0 EndX=23.4965 EndY=4 EndZ=0
    g8: LineSegment StartX=-24 StartY=4 StartZ=0 EndX=-25.7965 EndY=4 EndZ=0
    g9: LineSegment StartX=-25.7965 StartY=4 StartZ=0 EndX=-24 EndY=12 EndZ=0
    g10: LineSegment StartX=-24 StartY=12 StartZ=0 EndX=-24 EndY=4 EndZ=0
    g11: LineSegment StartX=-36 StartY=4 StartZ=0 EndX=-34.0101 EndY=4 EndZ=0
    g12: LineSegment StartX=-34.0101 StartY=4 StartZ=0 EndX=-32.2323 EndY=12 EndZ=0
    g13: LineSegment StartX=-32.2323 StartY=12 StartZ=0 EndX=-36 EndY=12 EndZ=0
    g14: LineSegment StartX=-36 StartY=12 StartZ=0 EndX=-36 EndY=4 EndZ=0
  constraints (19):
    c: Horizontal(g0)
    c: Coincident(g0,g1)
    c: Coincident(g1,g2)
    c: Coincident(g2,g3)
    c: Coincident(g3,g0)
    c: Horizontal(g4)
    c: Coincident(g4,g5)
    c: Coincident(g5,g6)
    c: Coincident(g6,g7)
    c: Coincident(g7,g4)
    c: Horizontal(g8)
    c: Coincident(g8,g9)
    c: Coincident(g9,g10)
    c: Coincident(g10,g8)
    c: Horizontal(g11)
    c: Coincident(g11,g12)
    c: Coincident(g12,g13)
    c: Coincident(g13,g14)
    c: Coincident(g14,g11)
FEATURE [PartDesign::Pocket] Pocket018
  BaseFeature = -> Pad015
  Length = 8
  Length2 = 100
  Profile = -> Sketch038
  Type = 0
FEATURE [Sketcher::SketchObject] Sketch039
  FullyConstrained = true
  MapMode = 5
  Placement = pos=(6,0,0) rot=(0.57735,0.57735,0.57735;2.0944rad)
  Support = -> [Pocket018]
  sketch-geometry (2):
    g0: Circle CenterX=-29 CenterY=7.95 CenterZ=0 NormalX=0 NormalY=0 NormalZ=1 AngleXU=0 Radius=1.5
    g1: Circle CenterX=29 CenterY=7.95 CenterZ=0 NormalX=0 NormalY=0 NormalZ=1 AngleXU=0 Radius=1.5
  constraints (5):
    c: Radius(g1) = 1.5
    c: Equal(g1,g0)
    c: Symmetric(g0,g1,g-2)
    c: DistanceX(g-2,g0) = -29
    c: DistanceY(g-1,g0) = 7.95
FEATURE [PartDesign::Pocket] Pocket019
  BaseFeature = -> Pocket018
  Length = 9
  Length2 = 100
  Profile = -> Sketch039
  Type = 0
FEATURE [PartDesign::Body] Body005  label="fixation_support_plaque_ecran"
  Group = -> [Sketch019,Pad003,Sketch037,Pad015,Sketch038,Pocket018,Sketch039,Pocket019]
  Origin = -> Origin005
  Tip = -> Pocket019
FEATURE [App::MeasureDistance] Distance  label="Distance: 19.76 mm"
  Distance = 19.7627
  P1 = (-15.2125,25.8857,88.3136)
  P2 = (1.05463e-05,38.5,88.4688)
FEATURE [Sketcher::SketchObject] Sketch040
  FullyConstrained = true
  MapMode = 5
  Support = -> [XY_Plane010]
  sketch-geometry (15):
    g0: LineSegment StartX=0 StartY=-17.91 StartZ=0 EndX=0 EndY=-26.91 EndZ=0
    g1: LineSegment StartX=0 StartY=-26.91 StartZ=0 EndX=0 EndY=-31.91 EndZ=0
    g2: LineSegment StartX=0 StartY=-31.91 StartZ=0 EndX=5 EndY=-31.91 EndZ=0
    g3: LineSegment StartX=5 StartY=-31.91 StartZ=0 EndX=5 EndY=-29.91 EndZ=0
    g4: LineSegment StartX=5 StartY=-29.91 StartZ=0 EndX=2 EndY=-29.91 EndZ=0
    g5: LineSegment StartX=2 StartY=-29.91 StartZ=0 EndX=2 EndY=-26.91 EndZ=0
    g6: LineSegment StartX=2 StartY=-26.91 StartZ=0 EndX=16 EndY=-26.91 EndZ=0
    g7: LineSegment StartX=16 StartY=-26.91 StartZ=0 EndX=16 EndY=-29.91 EndZ=0
    g8: LineSegment StartX=16 StartY=-29.91 StartZ=0 EndX=13 EndY=-29.91 EndZ=0
    g9: LineSegment StartX=13 StartY=-29.91 StartZ=0 EndX=13 EndY=-31.91 EndZ=0
    g10: LineSegment StartX=13 StartY=-31.91 StartZ=0 EndX=18 EndY=-31.91 EndZ=0
    g11: LineSegment StartX=18 StartY=-31.91 StartZ=0 EndX=18 EndY=-24.91 EndZ=0
    g12: LineSegment StartX=18 StartY=-24.91 StartZ=0 EndX=2 EndY=-24.91 EndZ=0
    g13: LineSegment StartX=2 StartY=-24.91 StartZ=0 EndX=2 EndY=-17.91 EndZ=0
    g14: LineSegment StartX=2 StartY=-17.91 StartZ=0 EndX=0 EndY=-17.91 EndZ=0
  constraints (45):
    c: Vertical(g1)
    c: Coincident(g1,g2)
    c: Horizontal(g2)
    c: Coincident(g2,g3)
    c: Vertical(g3)
    c: Coincident(g3,g4)
    c: Horizontal(g4)
    c: Coincident(g4,g5)
    c: Coincident(g5,g6)
    c: Horizontal(g6)
    c: Coincident(g6,g7)
    c: Vertical(g7)
    c: Coincident(g7,g8)
    c: Horizontal(g8)
    c: Coincident(g8,g9)
    c: Vertical(g9)
    c: Coincident(g9,g10)
    c: Horizontal(g10)
    c: Coincident(g10,g11)
    c: Vertical(g11)
    c: Coincident(g11,g12)
    c: Horizontal(g12)
    c: Coincident(g12,g13)
    c: Vertical(g13)
    c: Coincident(g13,g14)
    c: Coincident(g14,g0)
    c: Horizontal(g14)
    c: DistanceX(g6,g6) = 14
    c: DistanceY(g5,g5) = 3
    c: DistanceY(g7,g7) = 3
    c: Distance(g4,g1) = 2
    c: Distance(g6,g12) = 2
    c: Distance(g7,g11) = 2
    c: Distance(g3,g2) = 2
    c: Distance(g8,g10) = 2
    c: DistanceX(g4,g4) = 3
    c: DistanceX(g8,g8) = 3
    c: Vertical(g0)
    c: DistanceX(g14,g14) = 2
    c: DistanceY(g0,g0) = 9
    c: Vertical(g5)
    c: PointOnObject(g1,g-2)
    c: DistanceY(g-1,g0) = -26.91
    c: Coincident(g0,g1)
    c: DistanceY(g13,g13) = 7
FEATURE [PartDesign::Pad] Pad016
  Direction = (1,1,1)
  Length = 9
  Length2 = 100
  Profile = -> Sketch040
  Type = 0
FEATURE [Sketcher::SketchObject] Sketch041
  FullyConstrained = false
  MapMode = 5
  Placement = pos=(2,0,0) rot=(0.57735,0.57735,0.57735;2.0944rad)
  Support = -> [Pad016]
  sketch-geometry (1):
    g0: Circle CenterX=-21.91 CenterY=4.5 CenterZ=0 NormalX=0 NormalY=0 NormalZ=1 AngleXU=0 Radius=1.75
  constraints (2):
    c: DistanceY(g-1,g0) = 4.5
    c: Radius(g0) = 1.75
FEATURE [PartDesign::Pocket] Pocket020
  BaseFeature = -> Pad016
  Length = 12
  Length2 = 100
  Profile = -> Sketch041
  Type = 0
FEATURE [PartDesign::Fillet] Fillet014
  Base = -> Pocket020 [Edge7,Edge8]
  BaseFeature = -> Pocket020
  Radius = 4
  SupportTransform = false
FEATURE [PartDesign::Fillet] Fillet015
  Base = -> Fillet014 [Edge45,Edge50,Edge41,Edge48,Edge46]
  BaseFeature = -> Fillet014
  Radius = 1
  SupportTransform = false
FEATURE [PartDesign::Body] Body010  label="attache_leds"
  Group = -> [Sketch040,Pad016,Sketch041,Pocket020,Fillet014,Fillet015]
  Origin = -> Origin011
  Placement = pos=(6,-1,35) rot=(0,1,0;3.14159rad)
  Tip = -> Fillet015
FEATURE [Mesh::Feature] Mesh003  label="attache_leds (Meshed)"
FEATURE [Sketcher::SketchObject] Sketch042
  FullyConstrained = true
  MapMode = 5
  Support = -> [XY_Plane011]
  sketch-geometry (15):
    g0: LineSegment StartX=0 StartY=-17.91 StartZ=0 EndX=0 EndY=-26.91 EndZ=0
    g1: LineSegment StartX=0 StartY=-26.91 StartZ=0 EndX=0 EndY=-31.91 EndZ=0
    g2: LineSegment StartX=0 StartY=-31.91 StartZ=0 EndX=5 EndY=-31.91 EndZ=0
    g3: LineSegment StartX=5 StartY=-31.91 StartZ=0 EndX=5 EndY=-29.91 EndZ=0
    g4: LineSegment StartX=5 StartY=-29.91 StartZ=0 EndX=2 EndY=-29.91 EndZ=0
    g5: LineSegment StartX=2 StartY=-29.91 StartZ=0 EndX=2 EndY=-26.91 EndZ=0
    g6: LineSegment StartX=2 StartY=-26.91 StartZ=0 EndX=16 EndY=-26.91 EndZ=0
    g7: LineSegment StartX=16 StartY=-26.91 StartZ=0 EndX=16 EndY=-29.91 EndZ=0
    g8: LineSegment StartX=16 StartY=-29.91 StartZ=0 EndX=13 EndY=-29.91 EndZ=0
    g9: LineSegment StartX=13 StartY=-29.91 StartZ=0 EndX=13 EndY=-31.91 EndZ=0
    g10: LineSegment StartX=13 StartY=-31.91 StartZ=0 EndX=18 EndY=-31.91 EndZ=0
    g11: LineSegment StartX=18 StartY=-31.91 StartZ=0 EndX=18 EndY=-24.91 EndZ=0
    g12: LineSegment StartX=18 StartY=-24.91 StartZ=0 EndX=2 EndY=-24.91 EndZ=0
    g13: LineSegment StartX=2 StartY=-24.91 StartZ=0 EndX=2 EndY=-17.91 EndZ=0
    g14: LineSegment StartX=2 StartY=-17.91 StartZ=0 EndX=0 EndY=-17.91 EndZ=0
  constraints (45):
    c: Vertical(g1)
    c: Coincident(g1,g2)
    c: Horizontal(g2)
    c: Coincident(g2,g3)
    c: Vertical(g3)
    c: Coincident(g3,g4)
    c: Horizontal(g4)
    c: Coincident(g4,g5)
    c: Coincident(g5,g6)
    c: Horizontal(g6)
    c: Coincident(g6,g7)
    c: Vertical(g7)
    c: Coincident(g7,g8)
    c: Horizontal(g8)
    c: Coincident(g8,g9)
    c: Vertical(g9)
    c: Coincident(g9,g10)
    c: Horizontal(g10)
    c: Coincident(g10,g11)
    c: Vertical(g11)
    c: Coincident(g11,g12)
    c: Horizontal(g12)
    c: Coincident(g12,g13)
    c: Vertical(g13)
    c: Coincident(g13,g14)
    c: Coincident(g14,g0)
    c: Horizontal(g14)
    c: DistanceX(g6,g6) = 14
    c: DistanceY(g5,g5) = 3
    c: DistanceY(g7,g7) = 3
    c: Distance(g4,g1) = 2
    c: Distance(g6,g12) = 2
    c: Distance(g7,g11) = 2
    c: Distance(g3,g2) = 2
    c: Distance(g8,g10) = 2
    c: DistanceX(g4,g4) = 3
    c: DistanceX(g8,g8) = 3
    c: Vertical(g0)
    c: DistanceX(g14,g14) = 2
    c: DistanceY(g0,g0) = 9
    c: Vertical(g5)
    c: PointOnObject(g1,g-2)
    c: DistanceY(g-1,g0) = -26.91
    c: Coincident(g0,g1)
    c: DistanceY(g13,g13) = 7
FEATURE [PartDesign::Pad] Pad017
  Direction = (1,1,1)
  Length = 9
  Length2 = 100
  Profile = -> Sketch042
  Type = 0
FEATURE [Sketcher::SketchObject] Sketch043
  FullyConstrained = false
  MapMode = 5
  Placement = pos=(2,0,0) rot=(0.57735,0.57735,0.57735;2.0944rad)
  Support = -> [Pad017]
  sketch-geometry (1):
    g0: Circle CenterX=-21.91 CenterY=4.5 CenterZ=0 NormalX=0 NormalY=0 NormalZ=1 AngleXU=0 Radius=1.75
  constraints (2):
    c: DistanceY(g-1,g0) = 4.5
    c: Radius(g0) = 1.75
FEATURE [PartDesign::Pocket] Pocket021
  BaseFeature = -> Pad017
  Length = 12
  Length2 = 100
  Profile = -> Sketch043
  Type = 0
FEATURE [PartDesign::Fillet] Fillet016
  Base = -> Pocket021 [Edge7,Edge8]
  BaseFeature = -> Pocket021
  Radius = 4
  SupportTransform = false
FEATURE [PartDesign::Fillet] Fillet017
  Base = -> Fillet016 [Edge45,Edge50,Edge41,Edge48,Edge46]
  BaseFeature = -> Fillet016
  Radius = 1
  SupportTransform = false
FEATURE [PartDesign::Body] Body011  label="attache_leds001"
  Group = -> [Sketch042,Pad017,Sketch043,Pocket021,Fillet016,Fillet017]
  Origin = -> Origin012
  Placement = pos=(6,-1,128) rot=(0,1,0;3.14159rad)
  Tip = -> Fillet017
FEATURE [Sketcher::SketchObject] Sketch045
  FullyConstrained = true
  MapMode = 5
  Support = -> [XY_Plane012]
  sketch-geometry (15):
    g0: LineSegment StartX=0 StartY=-17.91 StartZ=0 EndX=0 EndY=-26.91 EndZ=0
    g1: LineSegment StartX=0 StartY=-26.91 StartZ=0 EndX=0 EndY=-31.91 EndZ=0
    g2: LineSegment StartX=0 StartY=-31.91 StartZ=0 EndX=5 EndY=-31.91 EndZ=0
    g3: LineSegment StartX=5 StartY=-31.91 StartZ=0 EndX=5 EndY=-29.91 EndZ=0
    g4: LineSegment StartX=5 StartY=-29.91 StartZ=0 EndX=2 EndY=-29.91 EndZ=0
    g5: LineSegment StartX=2 StartY=-29.91 StartZ=0 EndX=2 EndY=-26.91 EndZ=0
    g6: LineSegment StartX=2 StartY=-26.91 StartZ=0 EndX=16 EndY=-26.91 EndZ=0
    g7: LineSegment StartX=16 StartY=-26.91 StartZ=0 EndX=16 EndY=-29.91 EndZ=0
    g8: LineSegment StartX=16 StartY=-29.91 StartZ=0 EndX=13 EndY=-29.91 EndZ=0
    g9: LineSegment StartX=13 StartY=-29.91 StartZ=0 EndX=13 EndY=-31.91 EndZ=0
    g10: LineSegment StartX=13 StartY=-31.91 StartZ=0 EndX=18 EndY=-31.91 EndZ=0
    g11: LineSegment StartX=18 StartY=-31.91 StartZ=0 EndX=18 EndY=-24.91 EndZ=0
    g12: LineSegment StartX=18 StartY=-24.91 StartZ=0 EndX=2 EndY=-24.91 EndZ=0
    g13: LineSegment StartX=2 StartY=-24.91 StartZ=0 EndX=2 EndY=-17.91 EndZ=0
    g14: LineSegment StartX=2 StartY=-17.91 StartZ=0 EndX=0 EndY=-17.91 EndZ=0
  constraints (45):
    c: Vertical(g1)
    c: Coincident(g1,g2)
    c: Horizontal(g2)
    c: Coincident(g2,g3)
    c: Vertical(g3)
    c: Coincident(g3,g4)
    c: Horizontal(g4)
    c: Coincident(g4,g5)
    c: Coincident(g5,g6)
    c: Horizontal(g6)
    c: Coincident(g6,g7)
    c: Vertical(g7)
    c: Coincident(g7,g8)
    c: Horizontal(g8)
    c: Coincident(g8,g9)
    c: Vertical(g9)
    c: Coincident(g9,g10)
    c: Horizontal(g10)
    c: Coincident(g10,g11)
    c: Vertical(g11)
    c: Coincident(g11,g12)
    c: Horizontal(g12)
    c: Coincident(g12,g13)
    c: Vertical(g13)
    c: Coincident(g13,g14)
    c: Coincident(g14,g0)
    c: Horizontal(g14)
    c: DistanceX(g6,g6) = 14
    c: DistanceY(g5,g5) = 3
    c: DistanceY(g7,g7) = 3
    c: Distance(g4,g1) = 2
    c: Distance(g6,g12) = 2
    c: Distance(g7,g11) = 2
    c: Distance(g3,g2) = 2
    c: Distance(g8,g10) = 2
    c: DistanceX(g4,g4) = 3
    c: DistanceX(g8,g8) = 3
    c: Vertical(g0)
    c: DistanceX(g14,g14) = 2
    c: DistanceY(g0,g0) = 9
    c: Vertical(g5)
    c: PointOnObject(g1,g-2)
    c: DistanceY(g-1,g0) = -26.91
    c: Coincident(g0,g1)
    c: DistanceY(g13,g13) = 7
FEATURE [PartDesign::Pad] Pad018
  Direction = (1,1,1)
  Length = 9
  Length2 = 100
  Profile = -> Sketch045
  Type = 0
FEATURE [Sketcher::SketchObject] Sketch044
  FullyConstrained = false
  MapMode = 5
  Placement = pos=(2,0,0) rot=(0.57735,0.57735,0.57735;2.0944rad)
  Support = -> [Pad018]
  sketch-geometry (1):
    g0: Circle CenterX=-21.91 CenterY=4.5 CenterZ=0 NormalX=0 NormalY=0 NormalZ=1 AngleXU=0 Radius=1.75
  constraints (2):
    c: DistanceY(g-1,g0) = 4.5
    c: Radius(g0) = 1.75
FEATURE [PartDesign::Pocket] Pocket022
  BaseFeature = -> Pad018
  Length = 12
  Length2 = 100
  Profile = -> Sketch044
  Type = 0
FEATURE [PartDesign::Fillet] Fillet018
  Base = -> Pocket022 [Edge7,Edge8]
  BaseFeature = -> Pocket022
  Radius = 4
  SupportTransform = false
FEATURE [PartDesign::Fillet] Fillet019
  Base = -> Fillet018 [Edge45,Edge50,Edge41,Edge48,Edge46]
  BaseFeature = -> Fillet018
  Radius = 1
  SupportTransform = false
FEATURE [PartDesign::Body] Body012  label="attache_leds002"
  Group = -> [Sketch045,Pad018,Sketch044,Pocket022,Fillet018,Fillet019]
  Origin = -> Origin013
  Placement = pos=(6,1,119) rot=(0,0,-1;3.14159rad)
  Tip = -> Fillet019
FEATURE [Sketcher::SketchObject] Sketch046
  FullyConstrained = true
  MapMode = 5
  Support = -> [XY_Plane013]
  sketch-geometry (15):
    g0: LineSegment StartX=0 StartY=-17.91 StartZ=0 EndX=0 EndY=-26.91 EndZ=0
    g1: LineSegment StartX=0 StartY=-26.91 StartZ=0 EndX=0 EndY=-31.91 EndZ=0
    g2: LineSegment StartX=0 StartY=-31.91 StartZ=0 EndX=5 EndY=-31.91 EndZ=0
    g3: LineSegment StartX=5 StartY=-31.91 StartZ=0 EndX=5 EndY=-29.91 EndZ=0
    g4: LineSegment StartX=5 StartY=-29.91 StartZ=0 EndX=2 EndY=-29.91 EndZ=0
    g5: LineSegment StartX=2 StartY=-29.91 StartZ=0 EndX=2 EndY=-26.91 EndZ=0
    g6: LineSegment StartX=2 StartY=-26.91 StartZ=0 EndX=16 EndY=-26.91 EndZ=0
    g7: LineSegment StartX=16 StartY=-26.91 StartZ=0 EndX=16 EndY=-29.91 EndZ=0
    g8: LineSegment StartX=16 StartY=-29.91 StartZ=0 EndX=13 EndY=-29.91 EndZ=0
    g9: LineSegment StartX=13 StartY=-29.91 StartZ=0 EndX=13 EndY=-31.91 EndZ=0
    g10: LineSegment StartX=13 StartY=-31.91 StartZ=0 EndX=18 EndY=-31.91 EndZ=0
    g11: LineSegment StartX=18 StartY=-31.91 StartZ=0 EndX=18 EndY=-24.91 EndZ=0
    g12: LineSegment StartX=18 StartY=-24.91 StartZ=0 EndX=2 EndY=-24.91 EndZ=0
    g13: LineSegment StartX=2 StartY=-24.91 StartZ=0 EndX=2 EndY=-17.91 EndZ=0
    g14: LineSegment StartX=2 StartY=-17.91 StartZ=0 EndX=0 EndY=-17.91 EndZ=0
  constraints (45):
    c: Vertical(g1)
    c: Coincident(g1,g2)
    c: Horizontal(g2)
    c: Coincident(g2,g3)
    c: Vertical(g3)
    c: Coincident(g3,g4)
    c: Horizontal(g4)
    c: Coincident(g4,g5)
    c: Coincident(g5,g6)
    c: Horizontal(g6)
    c: Coincident(g6,g7)
    c: Vertical(g7)
    c: Coincident(g7,g8)
    c: Horizontal(g8)
    c: Coincident(g8,g9)
    c: Vertical(g9)
    c: Coincident(g9,g10)
    c: Horizontal(g10)
    c: Coincident(g10,g11)
    c: Vertical(g11)
    c: Coincident(g11,g12)
    c: Horizontal(g12)
    c: Coincident(g12,g13)
    c: Vertical(g13)
    c: Coincident(g13,g14)
    c: Coincident(g14,g0)
    c: Horizontal(g14)
    c: DistanceX(g6,g6) = 14
    c: DistanceY(g5,g5) = 3
    c: DistanceY(g7,g7) = 3
    c: Distance(g4,g1) = 2
    c: Distance(g6,g12) = 2
    c: Distance(g7,g11) = 2
    c: Distance(g3,g2) = 2
    c: Distance(g8,g10) = 2
    c: DistanceX(g4,g4) = 3
    c: DistanceX(g8,g8) = 3
    c: Vertical(g0)
    c: DistanceX(g14,g14) = 2
    c: DistanceY(g0,g0) = 9
    c: Vertical(g5)
    c: PointOnObject(g1,g-2)
    c: DistanceY(g-1,g0) = -26.91
    c: Coincident(g0,g1)
    c: DistanceY(g13,g13) = 7
FEATURE [PartDesign::Pad] Pad019
  Direction = (1,1,1)
  Length = 9
  Length2 = 100
  Profile = -> Sketch046
  Type = 0
FEATURE [Sketcher::SketchObject] Sketch047
  FullyConstrained = false
  MapMode = 5
  Placement = pos=(2,0,0) rot=(0.57735,0.57735,0.57735;2.0944rad)
  Support = -> [Pad019]
  sketch-geometry (1):
    g0: Circle CenterX=-21.91 CenterY=4.5 CenterZ=0 NormalX=0 NormalY=0 NormalZ=1 AngleXU=0 Radius=1.75
  constraints (2):
    c: DistanceY(g-1,g0) = 4.5
    c: Radius(g0) = 1.75
FEATURE [PartDesign::Pocket] Pocket023
  BaseFeature = -> Pad019
  Length = 12
  Length2 = 100
  Profile = -> Sketch047
  Type = 0
FEATURE [PartDesign::Fillet] Fillet020
  Base = -> Pocket023 [Edge7,Edge8]
  BaseFeature = -> Pocket023
  Radius = 4
  SupportTransform = false
FEATURE [PartDesign::Fillet] Fillet021
  Base = -> Fillet020 [Edge45,Edge50,Edge41,Edge48,Edge46]
  BaseFeature = -> Fillet020
  Radius = 1
  SupportTransform = false
FEATURE [PartDesign::Body] Body013  label="attache_leds003"
  Group = -> [Sketch046,Pad019,Sketch047,Pocket023,Fillet020,Fillet021]
  Origin = -> Origin014
  Placement = pos=(6,1,26) rot=(0,0,1;3.14159rad)
  Tip = -> Fillet021
